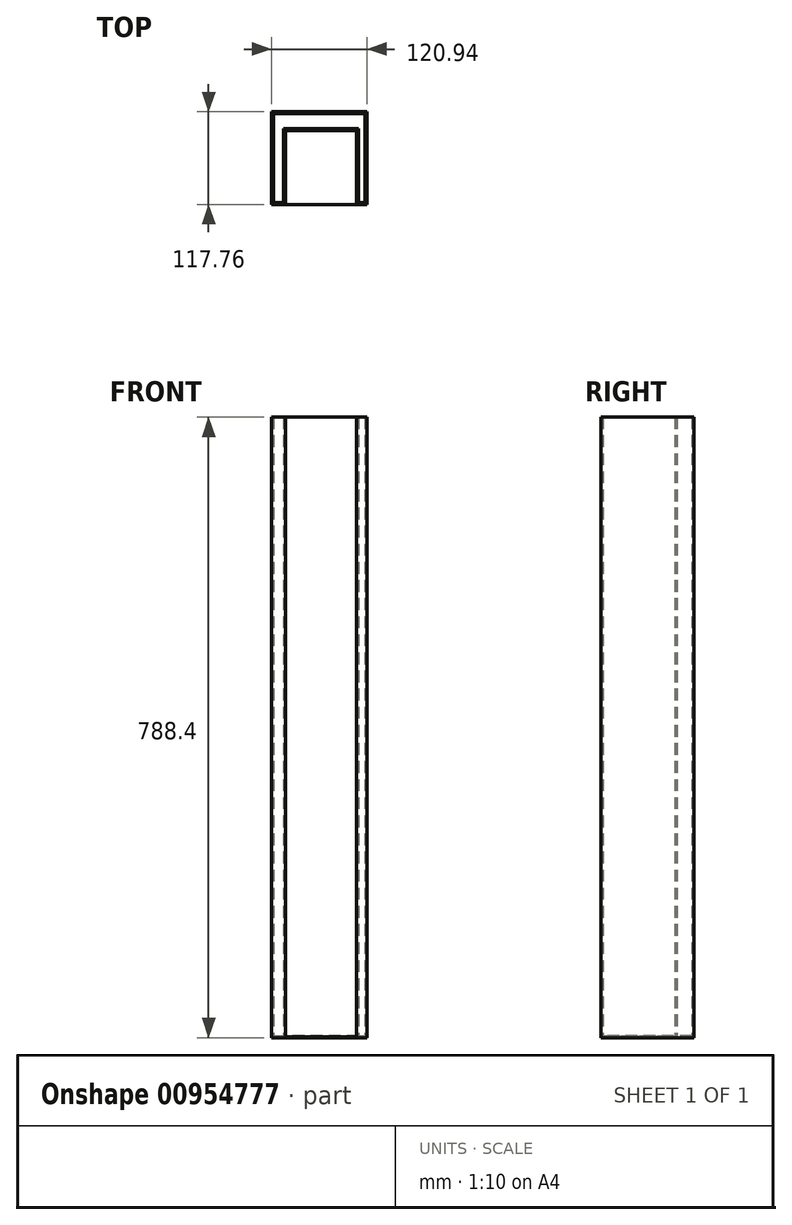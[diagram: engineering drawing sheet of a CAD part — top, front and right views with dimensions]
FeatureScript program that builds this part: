
annotation { "Feature Type Name" : "Feature", "Feature Type Description" : "" }
export const myFeature = defineFeature(function(context is Context, id is Id, definition is map)
    precondition{}
    {
        {
            var Q0;
            Q0=qCreatedBy(makeId("Top.planeOp"),FACE);
            var sketch = newSketch(context, id + "F0", { "sketchPlane" : qUnion([Q0])});
            skLineSegment(sketch, "E0.bottom", {"start": v(-60.47, 58.88) * mm, "end": v(60.47, 58.88) * mm});
            skLineSegment(sketch, "E0.top", {"start": v(-60.47, -58.88) * mm, "end": v(60.47, -58.88) * mm});
            skLineSegment(sketch, "E0.left", {"start": v(-60.47, 58.88) * mm, "end": v(-60.47, -58.88) * mm});
            skLineSegment(sketch, "E0.right", {"start": v(60.47, 58.88) * mm, "end": v(60.47, -58.88) * mm});
            skPoint(sketch, "E0.middle", {"position": v(0, 0) * mm});
            skSolve(sketch);
        }
        {
            var Q0;
            Q0 = qSketchRegion(id + "F0", true);
            var Q1;
            Q1=makeQuery(id+"F0.imprint","IMPRINT",FACE,{"disambiguationData":[TD([[makeQuery(id+"F0.imprint","IMPRINT",EDGE,{"derivedFrom":sQuery(id+"F0.wireOp",EDGE,"E0.bottom")}),-1.0]])]});
            extrude(context, id + "F1", {"entities" : qUnion([Q0, Q1]), "depth" : 1 * mm, "offsetDistance" : 25.4 * mm});
        }
        {
            var Q0;
            Q0=makeQuery(id+"F1.opExtrude","CAP_FACE",FACE,{"disambiguationData":[OSD([sQuery(id+"F0.wireOp",EDGE,"E0.bottom"),sQuery(id+"F0.wireOp",EDGE,"E0.top"),sQuery(id+"F0.wireOp",EDGE,"E0.left"),sQuery(id+"F0.wireOp",EDGE,"E0.right")])],"isStart":false});
            var sketch = newSketch(context, id + "F2", { "sketchPlane" : qUnion([Q0])});
            skLineSegment(sketch, "E1", {"start": v(-42.73, -58.88) * mm, "end": v(-42.73, 35.24) * mm});
            skLineSegment(sketch, "E2", {"start": v(-42.73, 35.24) * mm, "end": v(47.56, 35.24) * mm});
            skLineSegment(sketch, "E3", {"start": v(47.56, 35.24) * mm, "end": v(47.56, -58.88) * mm});
            skSolve(sketch);
        }
        {
            var Q0;
            {var subQ1=sQuery(id+"F2.wireOp",EDGE,"E1");Q0=makeQuery(id+"F2.imprint","IMPRINT",FACE,{"disambiguationData":[TD([[makeQuery(id+"F2.imprint","IMPRINT",EDGE,{"derivedFrom":subQ1}),1.0]])]});}
            var sketch = newSketch(context, id + "F3", { "sketchPlane" : qUnion([Q0])});
            skSolve(sketch);
        }
        {
            var Q0;
            {var subQ1=sQuery(id+"F2.wireOp",EDGE,"E1");Q0=makeQuery(id+"F3.imprint","IMPRINT",FACE,{"disambiguationData":[TD([[makeQuery(id+"F3.imprint","IMPRINT",EDGE,{"derivedFrom":makeQuery(id+"F2.imprint","IMPRINT",EDGE,{"derivedFrom":subQ1})}),1.0]])]});}
            extrude(context, id + "F4", {"entities" : qUnion([Q0]), "operationType" : NewBodyOperationType.ADD, "depth" : 25.4 * mm, "offsetDistance" : 25.4 * mm});
        }
        {
            var Q0;
            Q0=makeQuery(id+"F4.opExtrude","CAP_FACE",FACE,{"disambiguationData":[OSD([sQuery(id+"F0.wireOp",EDGE,"E0.bottom"),sQuery(id+"F0.wireOp",EDGE,"E0.top"),sQuery(id+"F0.wireOp",EDGE,"E0.left"),sQuery(id+"F0.wireOp",EDGE,"E0.right"),sQuery(id+"F2.wireOp",EDGE,"E1"),sQuery(id+"F2.wireOp",EDGE,"E2"),sQuery(id+"F2.wireOp",EDGE,"E3")])],"isStart":false});
            extrude(context, id + "F5", {"entities" : qUnion([Q0]), "operationType" : NewBodyOperationType.ADD, "depth" : 762 * mm, "offsetDistance" : 25.4 * mm});
        }
        {
            var Q0;
            Q0=makeQuery(id+"F5.opExtrude","CAP_FACE",FACE,{"disambiguationData":[OSD([sQuery(id+"F0.wireOp",EDGE,"E0.bottom"),sQuery(id+"F0.wireOp",EDGE,"E0.top"),sQuery(id+"F0.wireOp",EDGE,"E0.left"),sQuery(id+"F0.wireOp",EDGE,"E0.right"),sQuery(id+"F2.wireOp",EDGE,"E1"),sQuery(id+"F2.wireOp",EDGE,"E2"),sQuery(id+"F2.wireOp",EDGE,"E3")])],"isStart":false});
            shell(context, id + "F6", {"entities" : qUnion([Q0]), "thickness" : 2.54 * mm});
        }
    });
